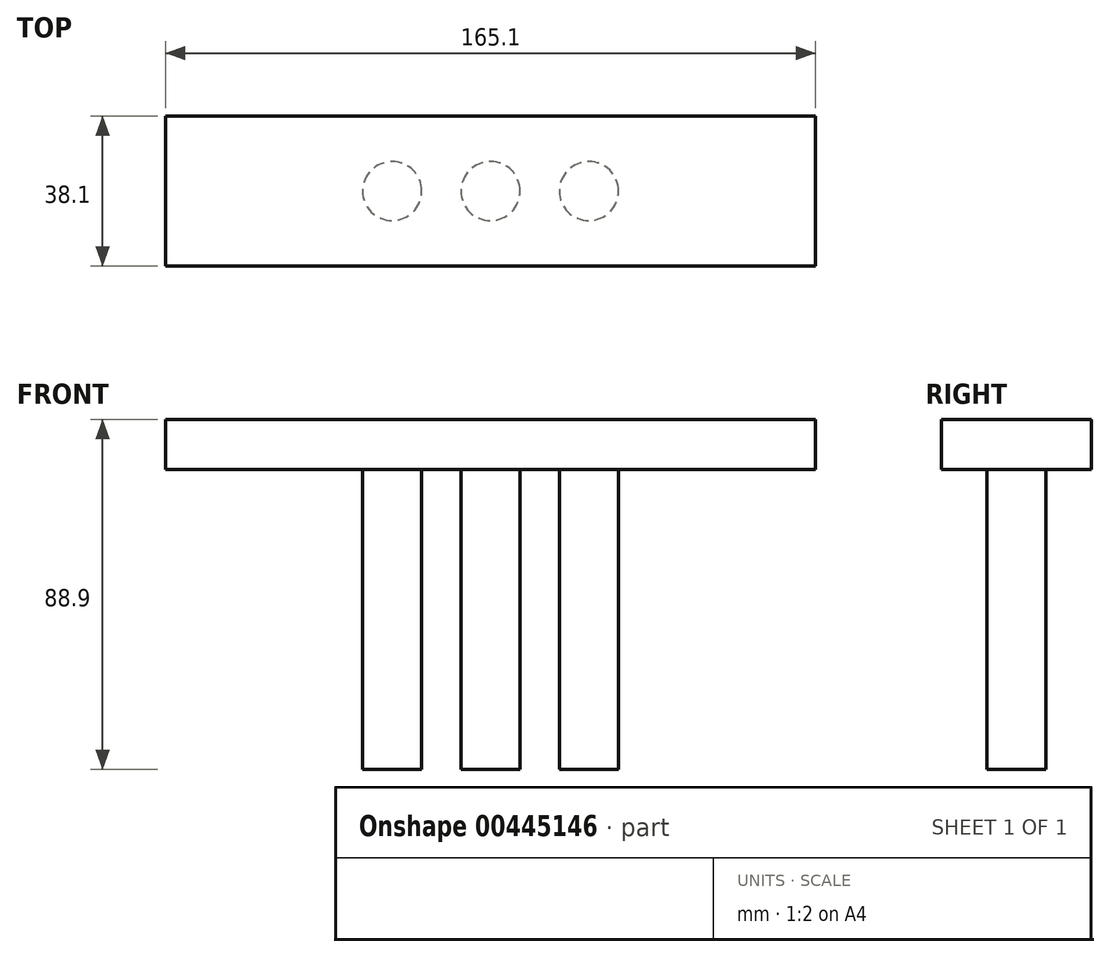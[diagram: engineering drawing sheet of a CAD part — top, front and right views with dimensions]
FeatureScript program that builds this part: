
annotation { "Feature Type Name" : "Feature", "Feature Type Description" : "" }
export const myFeature = defineFeature(function(context is Context, id is Id, definition is map)
    precondition{}
    {
        {
            var Q0;
            Q0=qCreatedBy(makeId("Top.planeOp"),FACE);
            var sketch = newSketch(context, id + "F0", { "sketchPlane" : qUnion([Q0])});
            skLineSegment(sketch, "E0.bottom", {"start": v(82.55, 19.05) * mm, "end": v(-82.55, 19.05) * mm});
            skLineSegment(sketch, "E0.top", {"start": v(82.55, -19.05) * mm, "end": v(-82.55, -19.05) * mm});
            skLineSegment(sketch, "E0.left", {"start": v(82.55, 19.05) * mm, "end": v(82.55, -19.05) * mm});
            skLineSegment(sketch, "E0.right", {"start": v(-82.55, 19.05) * mm, "end": v(-82.55, -19.05) * mm});
            skPoint(sketch, "E0.middle", {"position": v(0, 0) * mm});
            skCircle(sketch, "E1", {"center": v(0, 0) * mm, "radius": 7.5 * mm});
            skPoint(sketch, "E2", {"position": v(-25, 0) * mm});
            skCircle(sketch, "E3", {"center": v(-25, 0) * mm, "radius": 7.5 * mm});
            skLineSegment(sketch, "E4", {"start": v(-17.5, 0) * mm, "end": v(-7.5, 0) * mm});
            skPoint(sketch, "E5", {"position": v(25, 0) * mm});
            skCircle(sketch, "E6", {"center": v(25, 0) * mm, "radius": 7.5 * mm});
            skLineSegment(sketch, "E7", {"start": v(17.5, 0) * mm, "end": v(7.5, 0) * mm});
            skSolve(sketch);
        }
        {
            var Q0;
            Q0=makeQuery(id+"F0.imprint","IMPRINT",FACE,{"disambiguationData":[TD([[makeQuery(id+"F0.imprint","IMPRINT",EDGE,{"derivedFrom":sQuery(id+"F0.wireOp",EDGE,"E0.bottom")}),1.0]])]});
            var Q1;
            Q1=makeQuery(id+"F0.imprint","IMPRINT",FACE,{"disambiguationData":[TD([[makeQuery(id+"F0.imprint","IMPRINT",EDGE,{"derivedFrom":sQuery(id+"F0.wireOp",EDGE,"E3")}),1.0]])]});
            var Q2;
            {var subQ0=sQuery(id+"F0.wireOp",EDGE,"E1");var subQ1=makeQuery(id+"F0.imprint","IMPRINT",VERTEX,{"disambiguationData":[OD(0.0)],"derivedFrom":subQ0});Q2=makeQuery(id+"F0.imprint","IMPRINT",FACE,{"disambiguationData":[TD([[makeQuery(id+"F0.imprint","IMPRINT",EDGE,{"disambiguationData":[TD([[subQ1,1.0]])],"derivedFrom":subQ0}),1.0]])]});}
            var Q3;
            Q3=makeQuery(id+"F0.imprint","IMPRINT",FACE,{"disambiguationData":[TD([[makeQuery(id+"F0.imprint","IMPRINT",EDGE,{"derivedFrom":sQuery(id+"F0.wireOp",EDGE,"E6")}),1.0]])]});
            extrude(context, id + "F1", {"entities" : qUnion([Q0, Q1, Q2, Q3]), "depth" : 12.7 * mm});
        }
        {
            var Q0;
            Q0=makeQuery(id+"F0.imprint","IMPRINT",FACE,{"disambiguationData":[TD([[makeQuery(id+"F0.imprint","IMPRINT",EDGE,{"derivedFrom":sQuery(id+"F0.wireOp",EDGE,"E3")}),1.0]])]});
            var Q1;
            {var subQ0=sQuery(id+"F0.wireOp",EDGE,"E1");var subQ1=makeQuery(id+"F0.imprint","IMPRINT",VERTEX,{"disambiguationData":[OD(0.0)],"derivedFrom":subQ0});Q1=makeQuery(id+"F0.imprint","IMPRINT",FACE,{"disambiguationData":[TD([[makeQuery(id+"F0.imprint","IMPRINT",EDGE,{"disambiguationData":[TD([[subQ1,1.0]])],"derivedFrom":subQ0}),1.0]])]});}
            var Q2;
            Q2=makeQuery(id+"F0.imprint","IMPRINT",FACE,{"disambiguationData":[TD([[makeQuery(id+"F0.imprint","IMPRINT",EDGE,{"derivedFrom":sQuery(id+"F0.wireOp",EDGE,"E6")}),1.0]])]});
            extrude(context, id + "F2", {"entities" : qUnion([Q0, Q1, Q2]), "oppositeDirection" : true, "depth" : 76.2 * mm});
        }
    });
